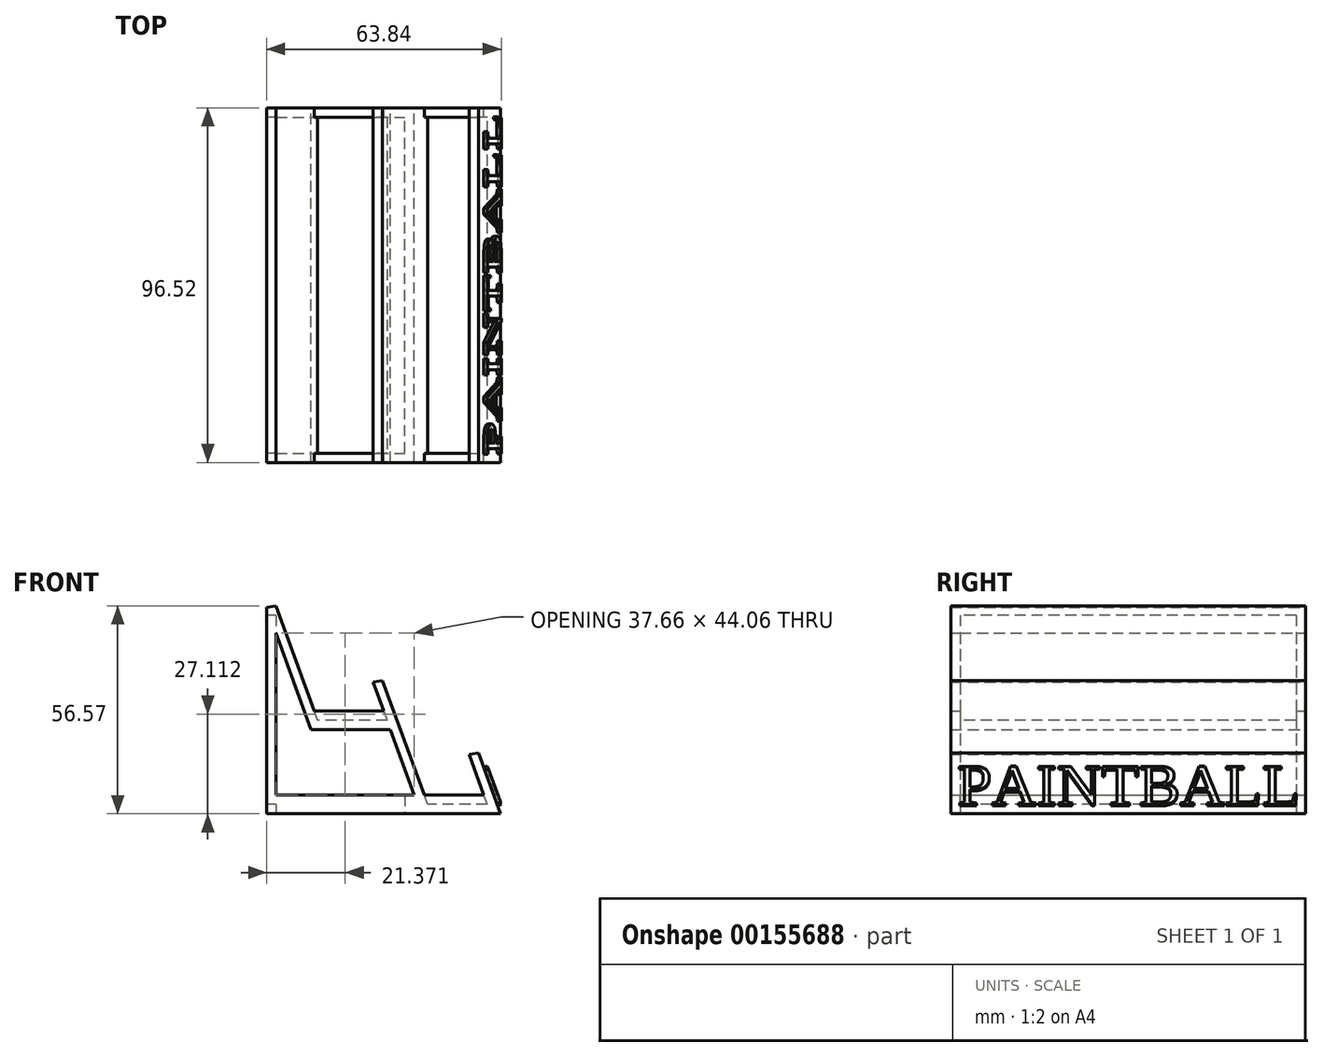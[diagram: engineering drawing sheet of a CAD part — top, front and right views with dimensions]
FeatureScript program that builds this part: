
annotation { "Feature Type Name" : "Feature", "Feature Type Description" : "" }
export const myFeature = defineFeature(function(context is Context, id is Id, definition is map)
    precondition{}
    {
        {
            var Q0;
            Q0=qCreatedBy(makeId("Front.planeOp"),FACE);
            var sketch = newSketch(context, id + "F0", { "sketchPlane" : qUnion([Q0])});
            skLineSegment(sketch, "E0", {"start": v(34.66, 0) * mm, "end": v(-29.02, 0) * mm});
            skLineSegment(sketch, "E1", {"start": v(34.66, 0) * mm, "end": v(28.63, 16.55) * mm});
            skLineSegment(sketch, "E2", {"start": v(11.18, 5.08) * mm, "end": v(4.71, 22.86) * mm});
            skLineSegment(sketch, "E3", {"start": v(4.71, 22.86) * mm, "end": v(-16.91, 22.86) * mm});
            skLineSegment(sketch, "E4", {"start": v(-16.91, 22.86) * mm, "end": v(-26.48, 49.14) * mm});
            skLineSegment(sketch, "E5", {"start": v(-29.02, 56.12) * mm, "end": v(-29.02, 0) * mm});
            skLineSegment(sketch, "E6", {"start": v(-26.48, 5.08) * mm, "end": v(11.18, 5.08) * mm});
            skLineSegment(sketch, "E7", {"start": v(-26.48, 5.08) * mm, "end": v(-26.48, 49.14) * mm});
            skLineSegment(sketch, "E8", {"start": v(-26.48, 56.57) * mm, "end": v(-16.06, 27.94) * mm});
            skLineSegment(sketch, "E9", {"start": v(-16.06, 27.94) * mm, "end": v(2.86, 27.94) * mm});
            skLineSegment(sketch, "E10", {"start": v(2.54, 36.25) * mm, "end": v(13.89, 5.08) * mm});
            skLineSegment(sketch, "E11", {"start": v(0, 35.8) * mm, "end": v(2.54, 36.25) * mm});
            skLineSegment(sketch, "E12", {"start": v(-29.02, 56.12) * mm, "end": v(-26.48, 56.57) * mm});
            skLineSegment(sketch, "E13", {"start": v(26.1, 16.1) * mm, "end": v(30.1, 5.08) * mm});
            skLineSegment(sketch, "E14", {"start": v(26.1, 16.1) * mm, "end": v(28.63, 16.55) * mm});
            skPoint(sketch, "E15.orphan", {"position": v(13.03, 0) * mm});
            skPoint(sketch, "E16.orphan", {"position": v(15.73, 0) * mm});
            skLineSegment(sketch, "E17.trimOffspring", {"start": v(13.89, 5.08) * mm, "end": v(30.1, 5.08) * mm});
            skLineSegment(sketch, "E18.trimOffspring", {"start": v(2.86, 27.94) * mm, "end": v(0, 35.8) * mm});
            skPoint(sketch, "E19.orphan", {"position": v(31.95, 0) * mm});
            skPoint(sketch, "E20.orphan", {"position": v(32.8, 5.08) * mm});
            skSolve(sketch);
        }
        {
            var Q0;
            Q0=qSketchRegion(id+"F0",true);
            extrude(context, id + "F1", {"entities" : qUnion([Q0]), "depth" : 96.52 * mm});
        }
        {
            var Q0;
            Q0=makeQuery(id+"F1.opExtrude","SWEPT_FACE",FACE,{"disambiguationData":[OSD([sQuery(id+"F0.wireOp",EDGE,"E9")])]});
            var Q1;
            Q1=makeQuery(id+"F1.opExtrude","SWEPT_FACE",FACE,{"disambiguationData":[OSD([sQuery(id+"F0.wireOp",EDGE,"E17.trimOffspring")])]});
            shell(context, id + "F2", {"entities" : qUnion([Q0, Q1]), "thickness" : 2.54 * mm});
        }
        {
            var Q0;
            Q0=makeQuery(id+"F1.opExtrude","SWEPT_FACE",FACE,{"disambiguationData":[OSD([sQuery(id+"F0.wireOp",EDGE,"E0")])]});
            var sketch = newSketch(context, id + "F3", { "sketchPlane" : qUnion([Q0])});
            skLineSegment(sketch, "E21.bottom", {"start": v(-26.48, 93.98) * mm, "end": v(8.64, 93.98) * mm});
            skLineSegment(sketch, "E21.top", {"start": v(-26.48, 2.54) * mm, "end": v(8.64, 2.54) * mm});
            skLineSegment(sketch, "E21.left", {"start": v(-26.48, 93.98) * mm, "end": v(-26.48, 2.54) * mm});
            skLineSegment(sketch, "E21.right", {"start": v(8.64, 93.98) * mm, "end": v(8.64, 2.54) * mm});
            skSolve(sketch);
        }
        {
            var Q0;
            Q0=makeQuery(id+"F3.imprint","IMPRINT",FACE,{"disambiguationData":[TD([[makeQuery(id+"F3.imprint","IMPRINT",EDGE,{"derivedFrom":sQuery(id+"F3.wireOp",EDGE,"E21.bottom")}),-1.0]])]});
            extrude(context, id + "F4", {"entities" : qUnion([Q0]), "operationType" : NewBodyOperationType.REMOVE, "oppositeDirection" : true, "depth" : 5.08 * mm});
        }
        {
            var Q0;
            Q0=makeQuery(id+"F1.opExtrude","SWEPT_FACE",FACE,{"disambiguationData":[OSD([sQuery(id+"F0.wireOp",EDGE,"E5")])]});
            var sketch = newSketch(context, id + "F5", { "sketchPlane" : qUnion([Q0])});
            skLineSegment(sketch, "E22.bottom", {"start": v(2.54, 54.03) * mm, "end": v(93.98, 54.03) * mm});
            skLineSegment(sketch, "E22.top", {"start": v(2.54, 2.54) * mm, "end": v(93.98, 2.54) * mm});
            skLineSegment(sketch, "E22.left", {"start": v(2.54, 54.03) * mm, "end": v(2.54, 2.54) * mm});
            skLineSegment(sketch, "E22.right", {"start": v(93.98, 54.03) * mm, "end": v(93.98, 2.54) * mm});
            skSolve(sketch);
        }
        {
            var Q0;
            Q0=qSketchRegion(id+"F5",true);
            extrude(context, id + "F6", {"entities" : qUnion([Q0]), "operationType" : NewBodyOperationType.REMOVE, "oppositeDirection" : true, "depth" : 2.54 * mm});
        }
        {
            var Q0;
            Q0=makeQuery(id+"F1.opExtrude","SWEPT_FACE",FACE,{"disambiguationData":[OSD([sQuery(id+"F0.wireOp",EDGE,"E1")])]});
            var sketch = newSketch(context, id + "F7", { "sketchPlane" : qUnion([Q0])});
            skText(sketch, "E23", { "text": "PAINTBALL", "fontName": "Tinos-Regular.ttf"});
            const initialGuessF7  = {"E23": [-0.0947, -0.0095, 1, 0, 0.01208]};
            skSetInitialGuess(sketch, initialGuessF7);
            skSolve(sketch);
        }
        {
            var Q0;
            Q0=qSketchRegion(id+"F7",true);
            extrude(context, id + "F8", {"entities" : qUnion([Q0]), "operationType" : NewBodyOperationType.ADD, "depth" : 1.02 * mm});
        }
    });
